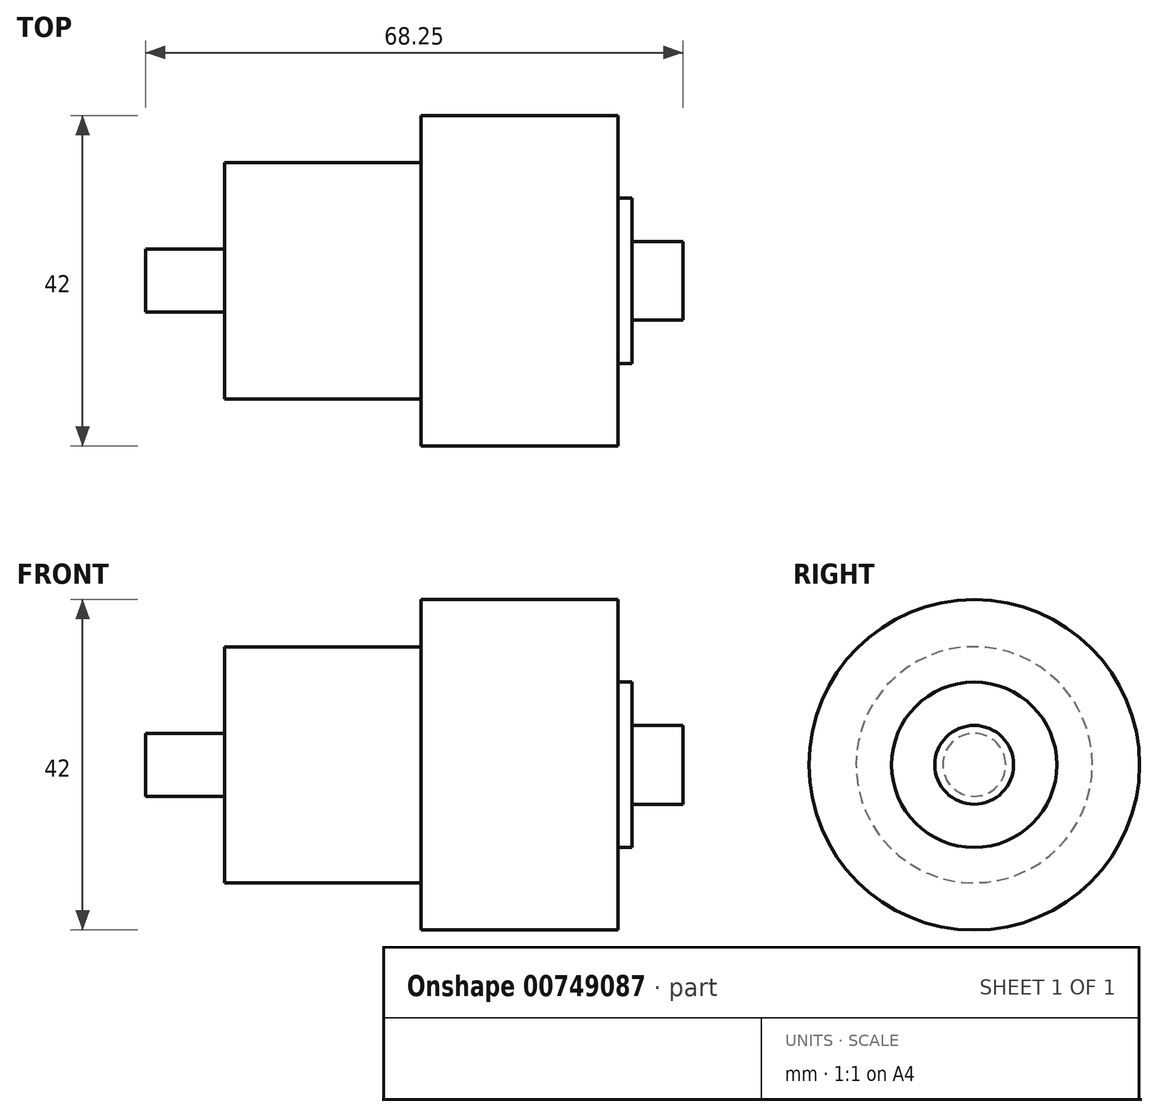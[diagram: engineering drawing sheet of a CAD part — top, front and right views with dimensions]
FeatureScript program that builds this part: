
annotation { "Feature Type Name" : "Feature", "Feature Type Description" : "" }
export const myFeature = defineFeature(function(context is Context, id is Id, definition is map)
    precondition{}
    {
        {
            var Q0;
            Q0=qCreatedBy(makeId("Front.planeOp"),FACE);
            var sketch = newSketch(context, id + "F0", { "sketchPlane" : qUnion([Q0])});
            skLineSegment(sketch, "E0", {"start": v(0, 0) * mm, "end": v(0, 4) * mm});
            skLineSegment(sketch, "E1", {"start": v(0, 4) * mm, "end": v(10, 4) * mm});
            skLineSegment(sketch, "E2", {"start": v(10, 4) * mm, "end": v(10, 15) * mm});
            skLineSegment(sketch, "E3", {"start": v(10, 15) * mm, "end": v(35, 15) * mm});
            skLineSegment(sketch, "E4", {"start": v(35, 15) * mm, "end": v(35, 21) * mm});
            skLineSegment(sketch, "E5", {"start": v(35, 21) * mm, "end": v(60, 21) * mm});
            skLineSegment(sketch, "E6", {"start": v(60, 21) * mm, "end": v(60, 10.5) * mm});
            skLineSegment(sketch, "E7", {"start": v(60, 10.5) * mm, "end": v(61.75, 10.5) * mm});
            skLineSegment(sketch, "E8", {"start": v(61.75, 10.5) * mm, "end": v(61.75, 5) * mm});
            skLineSegment(sketch, "E9", {"start": v(61.75, 5) * mm, "end": v(68.25, 5) * mm});
            skLineSegment(sketch, "E10", {"start": v(68.25, 5) * mm, "end": v(68.25, 0) * mm});
            skLineSegment(sketch, "E11", {"start": v(68.25, 0) * mm, "end": v(0, 0) * mm});
            skLineSegment(sketch, "E12", {"start": v(0, 0) * mm, "end": v(78.53, 0) * mm, "construction": true});
            skSolve(sketch);
        }
        {
            var Q0;
            Q0=makeQuery(id+"F0.imprint","IMPRINT",FACE,{"disambiguationData":[TD([[makeQuery(id+"F0.imprint","IMPRINT",EDGE,{"derivedFrom":sQuery(id+"F0.wireOp",EDGE,"E0")}),-1.0]])]});
            var Q1;
            Q1=sQuery(id+"F0.wireOp",EDGE,"E12");
            revolve(context, id + "F1", {"surfaceOperationType" : NewSurfaceOperationType.NEW, "entities" : qUnion([Q0]), "axis" : qUnion([Q1]), "revolveType" : RevolveType.FULL});
        }
    });
